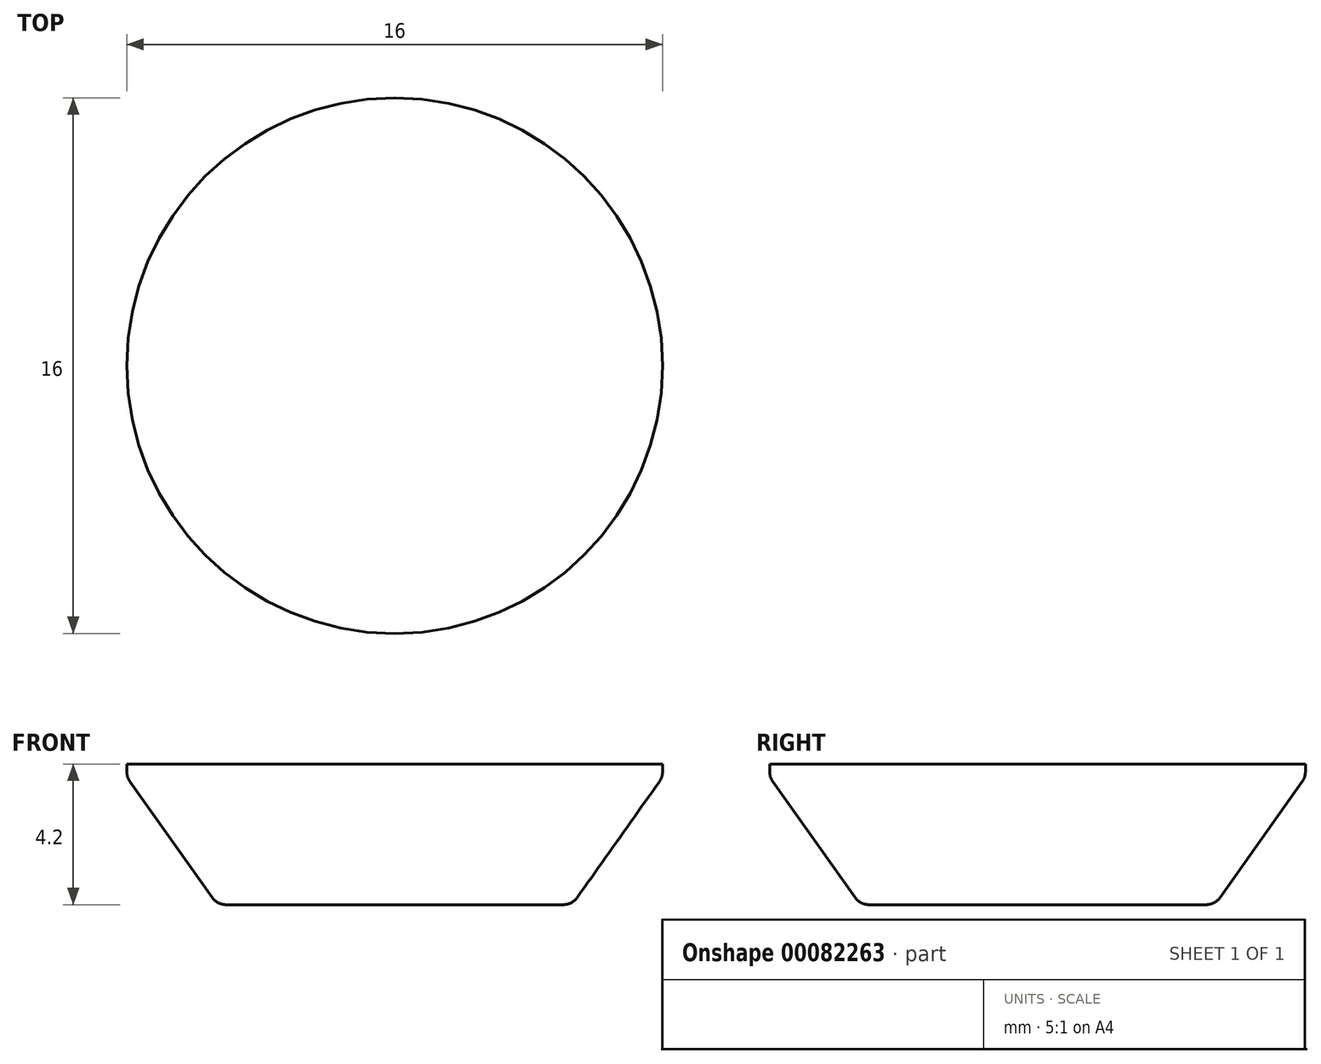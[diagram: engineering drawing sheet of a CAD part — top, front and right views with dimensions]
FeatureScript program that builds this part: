
annotation { "Feature Type Name" : "Feature", "Feature Type Description" : "" }
export const myFeature = defineFeature(function(context is Context, id is Id, definition is map)
    precondition{}
    {
        {
            var Q0;
            Q0=qCreatedBy(makeId("Front.planeOp"),FACE);
            var sketch = newSketch(context, id + "F0", { "sketchPlane" : qUnion([Q0])});
            skLineSegment(sketch, "E0.top", {"start": v(0, 4.2) * mm, "end": v(8, 4.2) * mm});
            skLineSegment(sketch, "E0.left", {"start": v(0, 0) * mm, "end": v(0, 4.2) * mm});
            skLineSegment(sketch, "E1", {"start": v(0, 0) * mm, "end": v(5.3, 0) * mm});
            skLineSegment(sketch, "E2", {"start": v(8, 4.2) * mm, "end": v(8, 3.8) * mm});
            skLineSegment(sketch, "E3", {"start": v(8, 3.8) * mm, "end": v(5.3, 0) * mm});
            skSolve(sketch);
        }
        {
            var Q0;
            Q0=makeQuery(id+"F0.imprint","IMPRINT",FACE,{"disambiguationData":[TD([[makeQuery(id+"F0.imprint","IMPRINT",EDGE,{"derivedFrom":sQuery(id+"F0.wireOp",EDGE,"E0.top")}),-1.0]])]});
            var Q1;
            Q1=sQuery(id+"F0.wireOp",EDGE,"E0.left");
            revolve(context, id + "F1", {"entities" : qUnion([Q0]), "axis" : qUnion([Q1]), "revolveType" : RevolveType.FULL});
        }
        {
            var Q0;
            Q0=makeQuery(id+"F1.opRevolve","SWEPT_EDGE",EDGE,{"disambiguationData":[OSD([sQuery(id+"F0.wireOp",EDGE,"E1"),sQuery(id+"F0.wireOp",EDGE,"E3")])]});
            fillet(context, id + "F2", {"entities" : qUnion([Q0]), "radius" : 0.5 * mm, "tangentPropagation" : true, "allowEdgeOverflow" : false});
        }
        {
            var Q0;
            Q0=makeQuery(id+"F1.opRevolve","SWEPT_EDGE",EDGE,{"disambiguationData":[OSD([sQuery(id+"F0.wireOp",EDGE,"E2"),sQuery(id+"F0.wireOp",EDGE,"E3")])]});
            fillet(context, id + "F3", {"entities" : qUnion([Q0]), "radius" : 0.5 * mm, "tangentPropagation" : true, "allowEdgeOverflow" : false});
        }
    });
